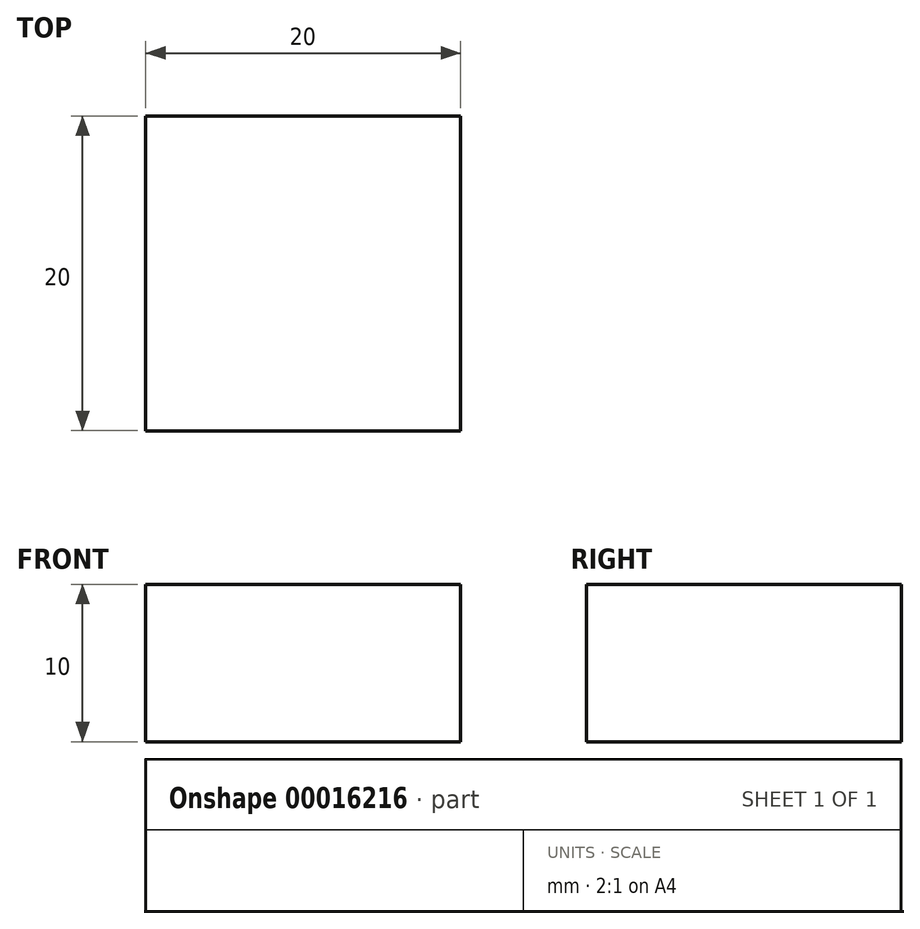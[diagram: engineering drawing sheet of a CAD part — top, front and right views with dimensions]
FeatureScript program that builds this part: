
annotation { "Feature Type Name" : "Feature", "Feature Type Description" : "" }
export const myFeature = defineFeature(function(context is Context, id is Id, definition is map)
    precondition{}
    {
        {
            var Q0;
            Q0=qCreatedBy(makeId("Top.planeOp"),FACE);
            var sketch = newSketch(context, id + "F0", { "sketchPlane" : qUnion([Q0])});
            skLineSegment(sketch, "E0.bottom", {"start": v(-9.58, -13.73) * mm, "end": v(10.42, -13.73) * mm});
            skLineSegment(sketch, "E0.top", {"start": v(-9.58, 6.27) * mm, "end": v(10.42, 6.27) * mm});
            skLineSegment(sketch, "E0.left", {"start": v(-9.58, -13.73) * mm, "end": v(-9.58, 6.27) * mm});
            skLineSegment(sketch, "E0.right", {"start": v(10.42, -13.73) * mm, "end": v(10.42, 6.27) * mm});
            skSolve(sketch);
        }
        {
            var Q0;
            Q0 = qSketchRegion(id + "F0", true);
            extrude(context, id + "F1", {"entities" : qUnion([Q0]), "depth" : 10 * mm});
        }
    });
